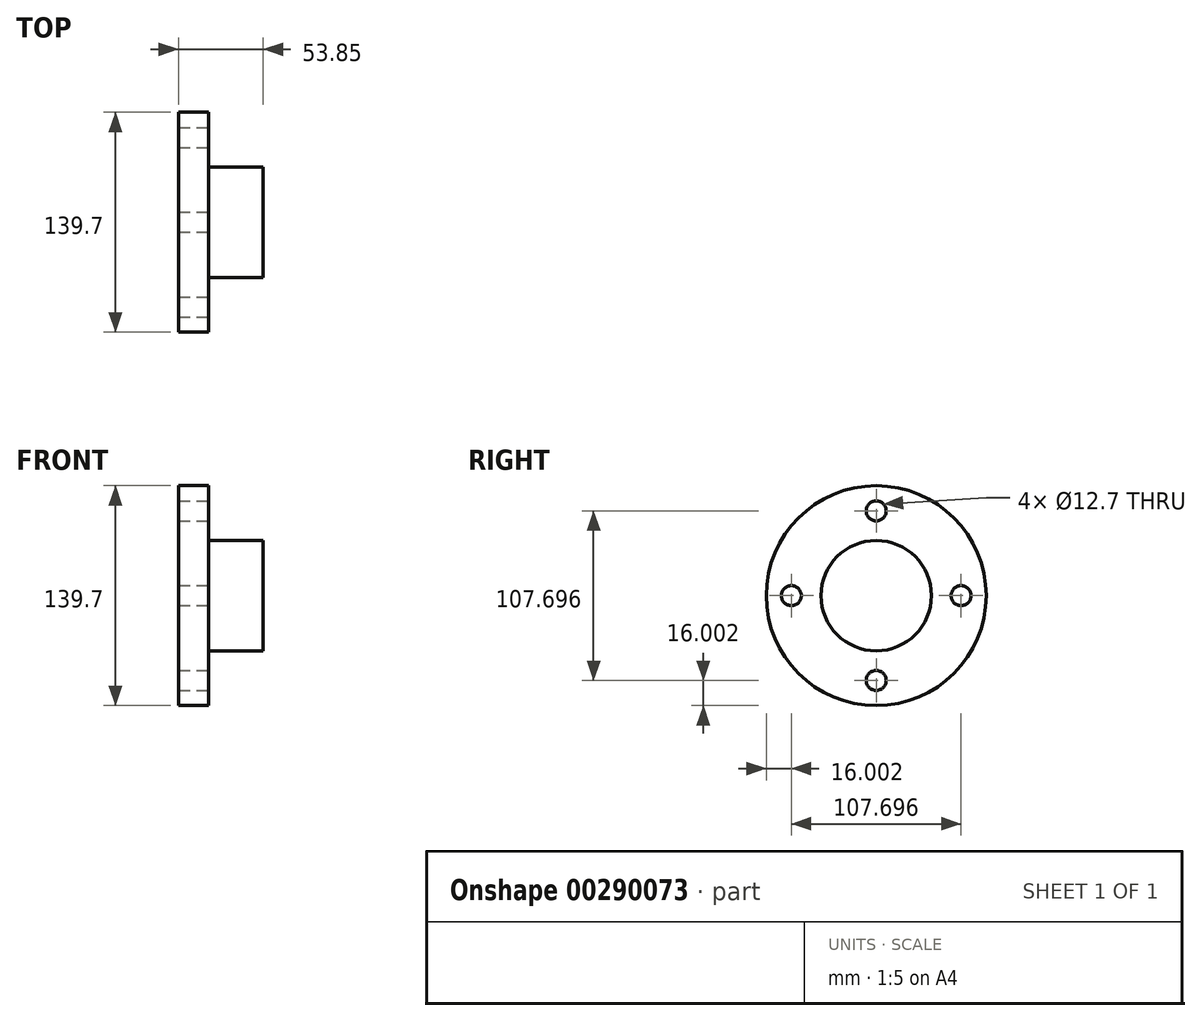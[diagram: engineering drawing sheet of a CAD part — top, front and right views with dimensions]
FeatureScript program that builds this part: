
annotation { "Feature Type Name" : "Feature", "Feature Type Description" : "" }
export const myFeature = defineFeature(function(context is Context, id is Id, definition is map)
    precondition{}
    {
        {
            var Q0;
            Q0=qCreatedBy(makeId("Front.planeOp"),FACE);
            var sketch = newSketch(context, id + "F0", { "sketchPlane" : qUnion([Q0])});
            skLineSegment(sketch, "E0", {"start": v(0, 0) * mm, "end": v(205.8, 0) * mm, "construction": true});
            skLineSegment(sketch, "E1", {"start": v(0, 0) * mm, "end": v(0, 69.85) * mm});
            skLineSegment(sketch, "E2", {"start": v(0, 69.85) * mm, "end": v(19.05, 69.85) * mm});
            skLineSegment(sketch, "E3", {"start": v(19.05, 69.85) * mm, "end": v(19.05, 35.05) * mm});
            skLineSegment(sketch, "E4", {"start": v(19.05, 35.05) * mm, "end": v(53.85, 35.05) * mm});
            skLineSegment(sketch, "E5", {"start": v(53.85, 35.05) * mm, "end": v(53.85, 0) * mm});
            skLineSegment(sketch, "E6", {"start": v(53.85, 0) * mm, "end": v(0, 0) * mm});
            skSolve(sketch);
        }
        {
            var Q0;
            Q0=makeQuery(id+"F0.imprint","IMPRINT",FACE,{"disambiguationData":[TD([[makeQuery(id+"F0.imprint","IMPRINT",EDGE,{"derivedFrom":sQuery(id+"F0.wireOp",EDGE,"E1")}),-1.0]])]});
            var Q1;
            Q1=sQuery(id+"F0.wireOp",EDGE,"E0");
            revolve(context, id + "F1", {"entities" : qUnion([Q0]), "axis" : qUnion([Q1]), "revolveType" : RevolveType.FULL});
        }
        {
            var Q0;
            Q0=makeQuery(id+"F1.opRevolve","SWEPT_FACE",FACE,{"disambiguationData":[OSD([sQuery(id+"F0.wireOp",EDGE,"E3")])]});
            var sketch = newSketch(context, id + "F2", { "sketchPlane" : qUnion([Q0])});
            skCircle(sketch, "E7", {"center": v(0, 0) * mm, "radius": 53.85 * mm, "construction": true});
            skCircle(sketch, "E8", {"center": v(0, 53.85) * mm, "radius": 6.35 * mm});
            skSolve(sketch);
        }
        {
            var Q0;
            Q0=makeQuery(id+"F2.imprint","IMPRINT",FACE,{"disambiguationData":[TD([[makeQuery(id+"F2.imprint","IMPRINT",EDGE,{"derivedFrom":sQuery(id+"F2.wireOp",EDGE,"E8")}),1.0]])]});
            var Q1;
            Q1=sQuery(id+"F2.wireOp",EDGE,"E8");
            extrude(context, id + "F3", {"entities" : qUnion([Q0]), "operationType" : NewBodyOperationType.REMOVE, "surfaceEntities" : qUnion([Q1]), "endBound" : BoundingType.THROUGH_ALL, "oppositeDirection" : true, "depth" : 25.4 * mm});
        }
        {
            var Q0;
            Q0=makeQuery(id+"F1.opRevolve","SWEPT_BODY",BODY,{"disambiguationData":[OSD([sQuery(id+"F0.wireOp",EDGE,"E1"),sQuery(id+"F0.wireOp",EDGE,"E2"),sQuery(id+"F0.wireOp",EDGE,"E3"),sQuery(id+"F0.wireOp",EDGE,"E4"),sQuery(id+"F0.wireOp",EDGE,"E5"),sQuery(id+"F0.wireOp",EDGE,"E6")])]});
            var Q1;
            Q1=makeQuery(id+"F1.opRevolve","SWEPT_EDGE",EDGE,{"disambiguationData":[OSD([sQuery(id+"F0.wireOp",EDGE,"E1"),sQuery(id+"F0.wireOp",EDGE,"E2")])]});
            circularPattern(context, id + "F4", {"entities" : qUnion([Q0]), "axis" : qUnion([Q1]), "angle" : 360 * degree, "instanceCount" : 4, "equalSpace" : true});
        }
    });
